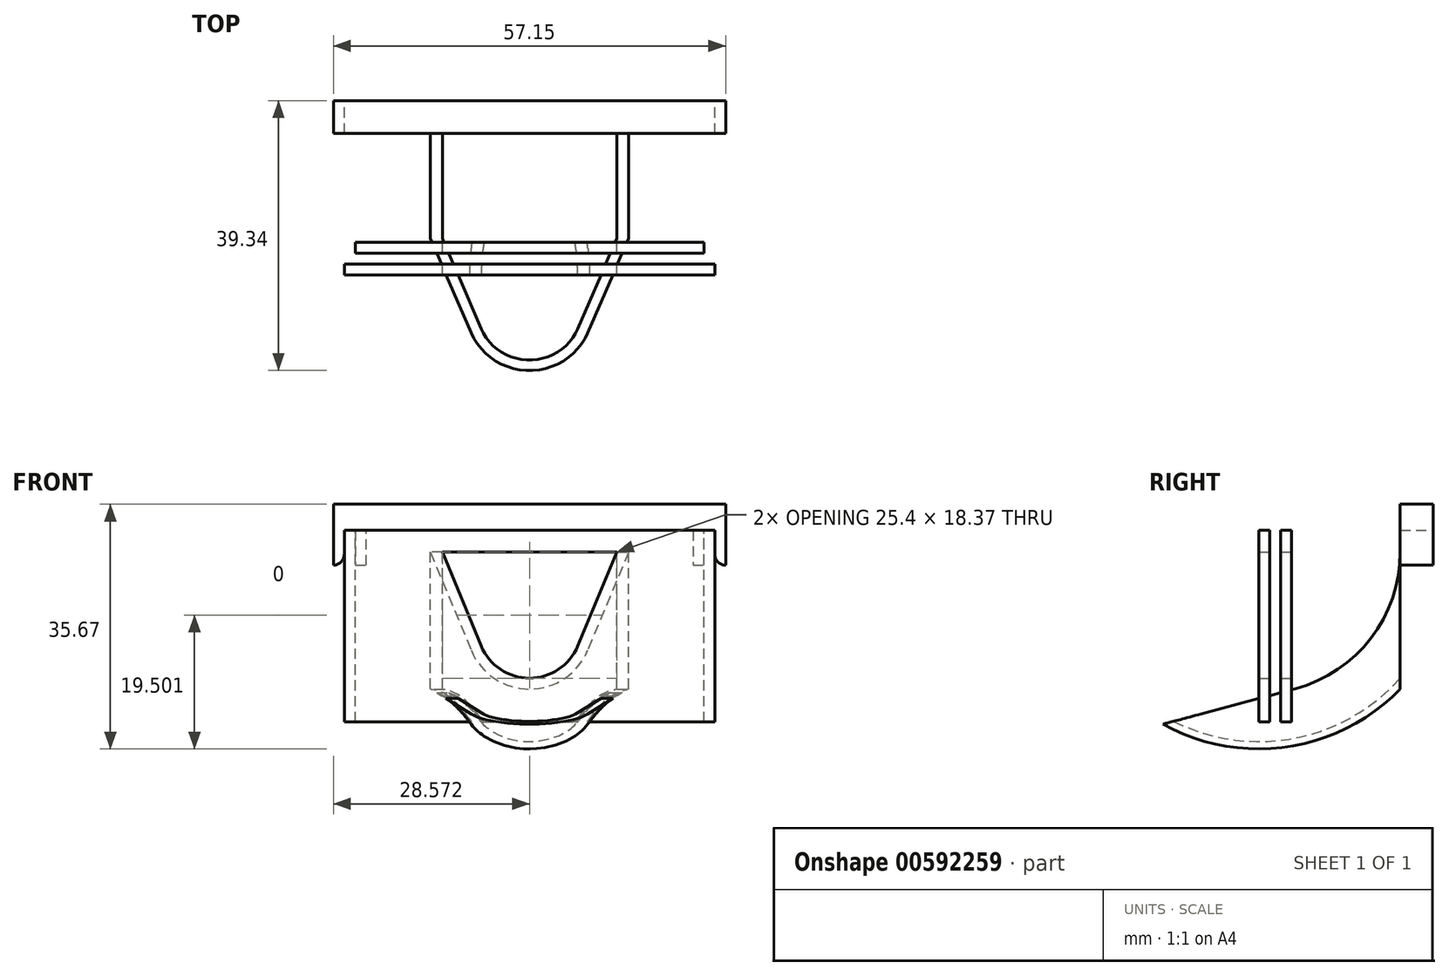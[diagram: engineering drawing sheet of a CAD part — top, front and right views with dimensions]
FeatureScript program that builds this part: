
annotation { "Feature Type Name" : "Feature", "Feature Type Description" : "" }
export const myFeature = defineFeature(function(context is Context, id is Id, definition is map)
    precondition{}
    {
        {
            var Q0;
            Q0=qCreatedBy(makeId("Front.planeOp"),FACE);
            var sketch = newSketch(context, id + "F0", { "sketchPlane" : qUnion([Q0])});
            skLineSegment(sketch, "E0", {"start": v(0, 0) * mm, "end": v(0, 5.08) * mm});
            skLineSegment(sketch, "E1", {"start": v(0, 5.08) * mm, "end": v(47.63, 5.08) * mm});
            skLineSegment(sketch, "E2", {"start": v(47.63, 5.08) * mm, "end": v(47.63, 0) * mm});
            skLineSegment(sketch, "E3", {"start": v(47.63, 0) * mm, "end": v(49.21, 0) * mm});
            skLineSegment(sketch, "E4", {"start": v(49.21, 0) * mm, "end": v(49.21, 5.08) * mm});
            skLineSegment(sketch, "E5", {"start": v(49.21, 5.08) * mm, "end": v(50.8, 5.08) * mm});
            skLineSegment(sketch, "E6", {"start": v(50.8, 5.08) * mm, "end": v(50.8, 0) * mm});
            skLineSegment(sketch, "E7", {"start": v(50.8, 0) * mm, "end": v(52.39, 0) * mm});
            skLineSegment(sketch, "E8", {"start": v(52.39, 0) * mm, "end": v(52.39, 8.9) * mm});
            skLineSegment(sketch, "E9", {"start": v(52.39, 8.9) * mm, "end": v(-4.76, 8.89) * mm});
            skLineSegment(sketch, "E10", {"start": v(-4.76, 8.89) * mm, "end": v(-4.76, 0) * mm});
            skLineSegment(sketch, "E11", {"start": v(-4.76, 0) * mm, "end": v(-3.17, 0) * mm});
            skLineSegment(sketch, "E12", {"start": v(-3.17, 0) * mm, "end": v(-3.17, 5.08) * mm});
            skLineSegment(sketch, "E13", {"start": v(-3.17, 5.08) * mm, "end": v(-1.59, 5.08) * mm});
            skLineSegment(sketch, "E14", {"start": v(-1.59, 5.08) * mm, "end": v(-1.59, 0) * mm});
            skLineSegment(sketch, "E15", {"start": v(-1.59, 0) * mm, "end": v(0, 0) * mm});
            skSolve(sketch);
        }
        {
            var Q0;
            Q0 = qSketchRegion(id + "F0", true);
            extrude(context, id + "F1", {"entities" : qUnion([Q0]), "depth" : 13 / 406.4 * mm, "offsetDistance" : 25.4 * mm});
        }
        {
            var Q0;
            Q0=makeQuery(id+"F1.opExtrude","CAP_FACE",FACE,{"disambiguationData":[OSD([sQuery(id+"F0.wireOp",EDGE,"E0"),sQuery(id+"F0.wireOp",EDGE,"E1"),sQuery(id+"F0.wireOp",EDGE,"E2"),sQuery(id+"F0.wireOp",EDGE,"E3"),sQuery(id+"F0.wireOp",EDGE,"E4"),sQuery(id+"F0.wireOp",EDGE,"E5"),sQuery(id+"F0.wireOp",EDGE,"E6"),sQuery(id+"F0.wireOp",EDGE,"E7"),sQuery(id+"F0.wireOp",EDGE,"E8"),sQuery(id+"F0.wireOp",EDGE,"E9"),sQuery(id+"F0.wireOp",EDGE,"E10"),sQuery(id+"F0.wireOp",EDGE,"E11"),sQuery(id+"F0.wireOp",EDGE,"E12"),sQuery(id+"F0.wireOp",EDGE,"E13"),sQuery(id+"F0.wireOp",EDGE,"E14"),sQuery(id+"F0.wireOp",EDGE,"E15")])],"isStart":false});
            var sketch = newSketch(context, id + "F2", { "sketchPlane" : qUnion([Q0])});
            skLineSegment(sketch, "E16", {"start": v(-4.76, 8.89) * mm, "end": v(-4.76, 0) * mm});
            skLineSegment(sketch, "E17", {"start": v(-4.76, 0) * mm, "end": v(-3.17, 0) * mm});
            skLineSegment(sketch, "E18", {"start": v(-3.17, 0) * mm, "end": v(-3.17, 5.08) * mm});
            skLineSegment(sketch, "E19", {"start": v(-3.17, 5.08) * mm, "end": v(50.8, 5.08) * mm});
            skLineSegment(sketch, "E20", {"start": v(50.8, 5.08) * mm, "end": v(50.8, 0) * mm});
            skLineSegment(sketch, "E21", {"start": v(50.8, 0) * mm, "end": v(52.39, 0) * mm});
            skLineSegment(sketch, "E22", {"start": v(52.39, 0) * mm, "end": v(52.39, 8.9) * mm});
            skLineSegment(sketch, "E23", {"start": v(52.39, 8.9) * mm, "end": v(-4.76, 8.89) * mm});
            skSolve(sketch);
        }
        {
            var Q0;
            Q0 = qSketchRegion(id + "F2", true);
            extrude(context, id + "F3", {"entities" : qUnion([Q0]), "operationType" : NewBodyOperationType.ADD, "depth" : 4.76 * mm, "offsetDistance" : 25.4 * mm});
        }
        {
            var Q0;
            Q0=makeQuery(id+"F3.boolean.opBoolean","MERGE",FACE,{"derivedFrom":[makeQuery(id+"F1.opExtrude","SWEPT_FACE",FACE,{"disambiguationData":[OSD([sQuery(id+"F0.wireOp",EDGE,"E1")])]}),makeQuery(id+"F1.opExtrude","SWEPT_FACE",FACE,{"disambiguationData":[OSD([sQuery(id+"F0.wireOp",EDGE,"E5")])]}),makeQuery(id+"F1.opExtrude","SWEPT_FACE",FACE,{"disambiguationData":[OSD([sQuery(id+"F0.wireOp",EDGE,"E13")])]}),makeQuery(id+"F3.opExtrude","SWEPT_FACE",FACE,{"disambiguationData":[OSD([sQuery(id+"F2.wireOp",EDGE,"E19")])]})]});
            var sketch = newSketch(context, id + "F4", { "sketchPlane" : qUnion([Q0])});
            skLineSegment(sketch, "E24", {"start": v(-1.59, 20.64) * mm, "end": v(49.21, 20.64) * mm});
            skLineSegment(sketch, "E25", {"start": v(49.21, 20.64) * mm, "end": v(49.21, 22.23) * mm});
            skLineSegment(sketch, "E26", {"start": v(49.21, 22.23) * mm, "end": v(-1.59, 22.23) * mm});
            skLineSegment(sketch, "E27", {"start": v(-1.59, 22.23) * mm, "end": v(-1.59, 20.64) * mm});
            skLineSegment(sketch, "E28", {"start": v(-3.17, 25.4) * mm, "end": v(50.8, 25.4) * mm});
            skLineSegment(sketch, "E29", {"start": v(50.8, 25.4) * mm, "end": v(50.8, 23.81) * mm});
            skLineSegment(sketch, "E30", {"start": v(50.8, 23.81) * mm, "end": v(-3.17, 23.81) * mm});
            skLineSegment(sketch, "E31", {"start": v(-3.17, 23.81) * mm, "end": v(-3.17, 25.4) * mm});
            skSolve(sketch);
        }
        {
            var Q0;
            Q0 = qSketchRegion(id + "F4", true);
            extrude(context, id + "F5", {"entities" : qUnion([Q0]), "operationType" : NewBodyOperationType.ADD, "depth" : 27.94 * mm, "offsetDistance" : 25.4 * mm});
        }
        {
            var Q0;
            Q0=makeQuery(id+"F5.opExtrude","SWEPT_FACE",FACE,{"disambiguationData":[OSD([sQuery(id+"F4.wireOp",EDGE,"E24")])]});
            var sketch = newSketch(context, id + "F6", { "sketchPlane" : qUnion([Q0])});
            skLineSegment(sketch, "E32", {"start": v(-36.51, 1.9) * mm, "end": v(-11.11, 1.9) * mm});
            skLineSegment(sketch, "E33", {"start": v(-11.11, 1.9) * mm, "end": v(-16.77, -11.76) * mm});
            skLineSegment(sketch, "E34", {"start": v(-36.51, 1.9) * mm, "end": v(-30.85, -11.76) * mm});
            skArc(sketch, "E35", {"start": v(-30.85, -11.76) * mm, "mid": v(-23.81, -16.46) * mm, "end": v(-16.77, -11.76) * mm});
            skLineSegment(sketch, "E36", {"start": v(-23.81, -8.84) * mm, "end": v(-23.81, 5.08) * mm, "construction": true});
            skLineSegment(sketch, "E37", {"start": v(-11.11, 1.9) * mm, "end": v(-23.81, 5.08) * mm, "construction": true});
            skLineSegment(sketch, "E38", {"start": v(-23.81, 5.08) * mm, "end": v(-36.51, 1.9) * mm, "construction": true});
            skSolve(sketch);
        }
        {
            var Q0;
            Q0 = qSketchRegion(id + "F6", true);
            extrude(context, id + "F7", {"entities" : qUnion([Q0]), "operationType" : NewBodyOperationType.REMOVE, "oppositeDirection" : true, "depth" : 24.64 * mm, "offsetDistance" : 25.4 * mm});
        }
        {
            var Q0;
            Q0=makeQuery(id+"F5.boolean.opBoolean","MERGE",FACE,{"derivedFrom":[makeQuery(id+"F3.opExtrude","CAP_FACE",FACE,{"disambiguationData":[OSD([sQuery(id+"F2.wireOp",EDGE,"E16"),sQuery(id+"F2.wireOp",EDGE,"E17"),sQuery(id+"F2.wireOp",EDGE,"E18"),sQuery(id+"F2.wireOp",EDGE,"E19"),sQuery(id+"F2.wireOp",EDGE,"E20"),sQuery(id+"F2.wireOp",EDGE,"E21"),sQuery(id+"F2.wireOp",EDGE,"E22"),sQuery(id+"F2.wireOp",EDGE,"E23")])],"isStart":false}),makeQuery(id+"F5.opExtrude","SWEPT_FACE",FACE,{"disambiguationData":[OSD([sQuery(id+"F4.wireOp",EDGE,"E28")])]})]});
            var sketch = newSketch(context, id + "F8", { "sketchPlane" : qUnion([Q0])});
            skLineSegment(sketch, "E39", {"start": v(36.51, 1.9) * mm, "end": v(30.85, -11.76) * mm});
            skLineSegment(sketch, "E40", {"start": v(11.11, 1.9) * mm, "end": v(16.77, -11.76) * mm});
            skArc(sketch, "E41", {"start": v(16.77, -11.76) * mm, "mid": v(23.81, -16.46) * mm, "end": v(30.85, -11.76) * mm});
            skLineSegment(sketch, "E42", {"start": v(11.11, 1.9) * mm, "end": v(9.4, 1.9) * mm});
            skLineSegment(sketch, "E43", {"start": v(9.4, 1.9) * mm, "end": v(15.3, -12.37) * mm});
            skLineSegment(sketch, "E44", {"start": v(36.51, 1.9) * mm, "end": v(38.23, 1.9) * mm});
            skLineSegment(sketch, "E45", {"start": v(38.23, 1.9) * mm, "end": v(32.32, -12.37) * mm});
            skArc(sketch, "E46", {"start": v(15.3, -12.37) * mm, "mid": v(23.81, -18.05) * mm, "end": v(32.32, -12.37) * mm});
            skSolve(sketch);
        }
        {
            var Q0;
            Q0 = qSketchRegion(id + "F8", true);
            var Q1;
            Q1=makeQuery(id+"F7.boolean.opBoolean","INTERSECT",EDGE,{"derivedFrom":[makeQuery(id+"F5.boolean.opBoolean","MERGE",FACE,{"derivedFrom":[makeQuery(id+"F3.opExtrude","CAP_FACE",FACE,{"disambiguationData":[OSD([sQuery(id+"F2.wireOp",EDGE,"E16"),sQuery(id+"F2.wireOp",EDGE,"E17"),sQuery(id+"F2.wireOp",EDGE,"E18"),sQuery(id+"F2.wireOp",EDGE,"E19"),sQuery(id+"F2.wireOp",EDGE,"E20"),sQuery(id+"F2.wireOp",EDGE,"E21"),sQuery(id+"F2.wireOp",EDGE,"E22"),sQuery(id+"F2.wireOp",EDGE,"E23")])],"isStart":false}),makeQuery(id+"F5.opExtrude","SWEPT_FACE",FACE,{"disambiguationData":[OSD([sQuery(id+"F4.wireOp",EDGE,"E28")])]})]}),makeQuery(id+"F7.opExtrude","SWEPT_FACE",FACE,{"disambiguationData":[OSD([sQuery(id+"F6.wireOp",EDGE,"E32")])]})]});
            revolve(context, id + "F9", {"operationType" : NewBodyOperationType.ADD, "entities" : qUnion([Q0]), "axis" : qUnion([Q1]), "revolveType" : RevolveType.ONE_DIRECTION, "oppositeDirection" : true, "angle" : 75 * degree});
        }
        {
            var Q0;
            {var subQ0=sQuery(id+"F0.wireOp",EDGE,"E7");var subQ1=sQuery(id+"F2.wireOp",EDGE,"E21");Q0=makeQuery(id+"F5.boolean.opBoolean","SPLIT",EDGE,{"disambiguationData":[topologyDisambiguationEdgeConnected([makeQuery(id+"F5.opExtrude","SWEPT_FACE",FACE,{"disambiguationData":[OSD([sQuery(id+"F4.wireOp",EDGE,"E29")])]})])],"derivedFrom":makeQuery(id+"F3.boolean.opBoolean","MERGE",EDGE,{"derivedFrom":[makeQuery(id+"F1.opExtrude","SWEPT_EDGE",EDGE,{"disambiguationData":[OSD([sQuery(id+"F0.wireOp",EDGE,"E6"),subQ0])]}),makeQuery(id+"F3.opExtrude","SWEPT_EDGE",EDGE,{"disambiguationData":[OSD([sQuery(id+"F2.wireOp",EDGE,"E20"),subQ1])]})]})});}
            var Q1;
            {var subQ0=sQuery(id+"F0.wireOp",EDGE,"E11");var subQ1=sQuery(id+"F2.wireOp",EDGE,"E17");Q1=makeQuery(id+"F5.boolean.opBoolean","SPLIT",EDGE,{"disambiguationData":[topologyDisambiguationEdgeConnected([makeQuery(id+"F5.opExtrude","SWEPT_FACE",FACE,{"disambiguationData":[OSD([sQuery(id+"F4.wireOp",EDGE,"E31")])]})])],"derivedFrom":makeQuery(id+"F3.boolean.opBoolean","MERGE",EDGE,{"derivedFrom":[makeQuery(id+"F1.opExtrude","SWEPT_EDGE",EDGE,{"disambiguationData":[OSD([subQ0,sQuery(id+"F0.wireOp",EDGE,"E12")])]}),makeQuery(id+"F3.opExtrude","SWEPT_EDGE",EDGE,{"disambiguationData":[OSD([subQ1,sQuery(id+"F2.wireOp",EDGE,"E18")])]})]})});}
            fillet(context, id + "F10", {"entities" : qUnion([Q0, Q1]), "radius" : 1.59 * mm, "tangentPropagation" : true, "allowEdgeOverflow" : false});
        }
    });
